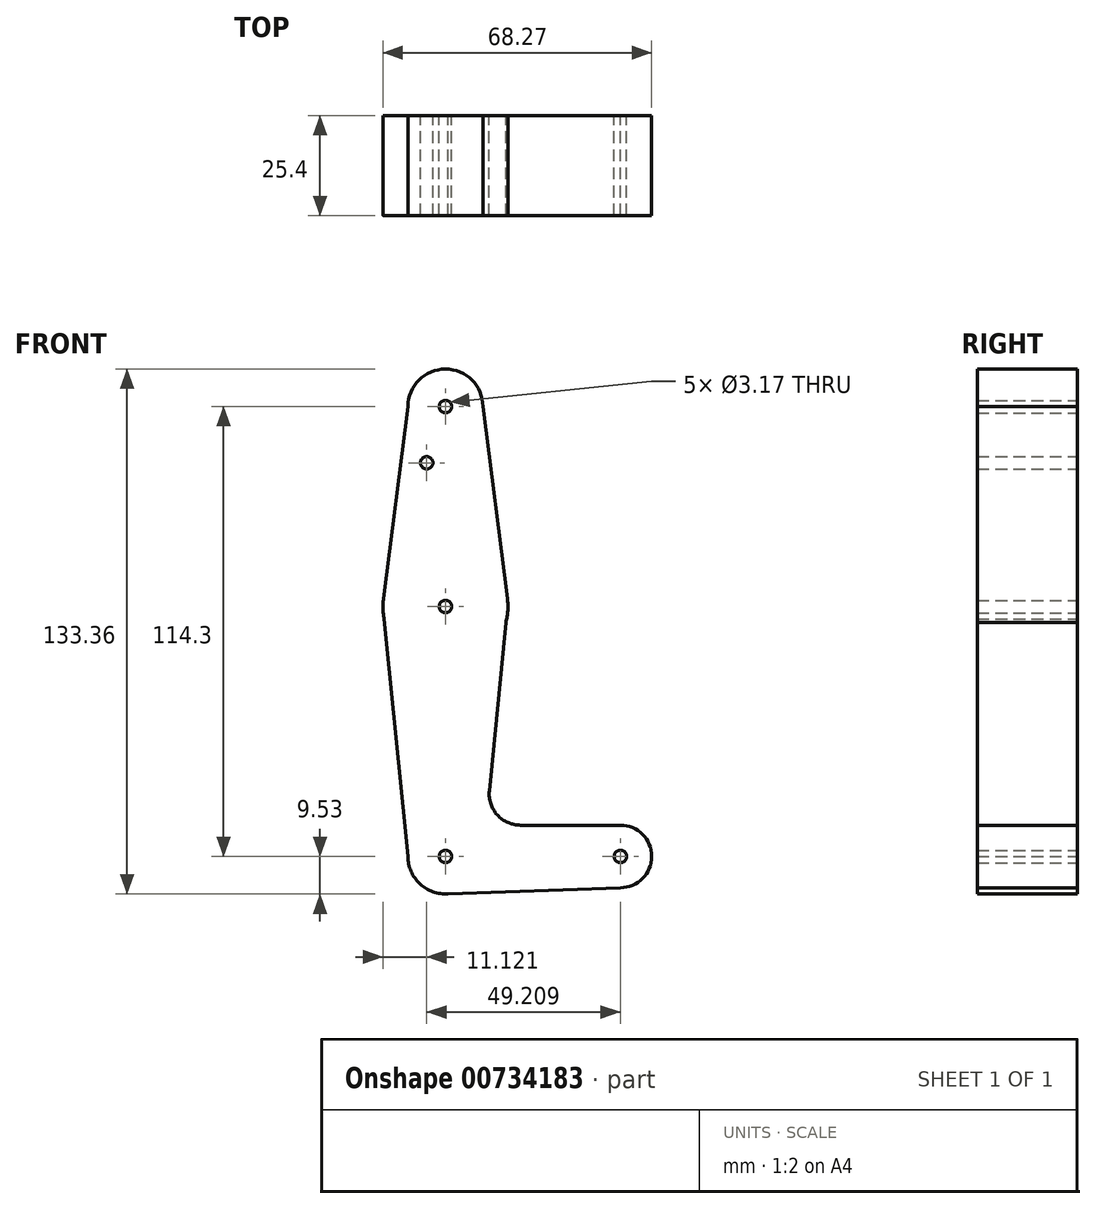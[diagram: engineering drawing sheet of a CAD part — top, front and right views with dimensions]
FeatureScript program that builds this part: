
annotation { "Feature Type Name" : "Feature", "Feature Type Description" : "" }
export const myFeature = defineFeature(function(context is Context, id is Id, definition is map)
    precondition{}
    {
        {
            var Q0;
            Q0=qCreatedBy(makeId("Front.planeOp"),FACE);
            var sketch = newSketch(context, id + "F0", { "sketchPlane" : qUnion([Q0])});
            skPoint(sketch, "E0.start.orphan", {"position": v(0, 0) * mm});
            skLineSegment(sketch, "E1", {"start": v(0, 0) * mm, "end": v(44.45, 0) * mm});
            skCircle(sketch, "E2", {"center": v(0, 114.3) * mm, "radius": 9.53 * mm});
            skCircle(sketch, "E3", {"center": v(0, 0) * mm, "radius": 9.53 * mm});
            skCircle(sketch, "E4", {"center": v(44.45, 0) * mm, "radius": 7.94 * mm});
            skCircle(sketch, "E5", {"center": v(0, 63.5) * mm, "radius": 15.88 * mm});
            skLineSegment(sketch, "E6", {"start": v(0, 0) * mm, "end": v(0, 114.3) * mm});
            skLineSegment(sketch, "E7", {"start": v(-9.52, 114.3) * mm, "end": v(-15.75, 65.5) * mm});
            skLineSegment(sketch, "E8", {"start": v(-15.88, 63.5) * mm, "end": v(-9.52, 0) * mm});
            skPoint(sketch, "E9.start.orphan", {"position": v(0, -9.53) * mm});
            skLineSegment(sketch, "E10", {"start": v(0, -9.53) * mm, "end": v(44.45, -7.94) * mm});
            skLineSegment(sketch, "E11", {"start": v(19.07, 7.94) * mm, "end": v(44.45, 7.94) * mm});
            skLineSegment(sketch, "E12", {"start": v(9.53, 114.3) * mm, "end": v(15.75, 65.5) * mm});
            skLineSegment(sketch, "E13", {"start": v(15.75, 63.5) * mm, "end": v(11.16, 16.66) * mm});
            skArc(sketch, "E14.filletArc", {"start": v(11.16, 16.66) * mm, "mid": v(13.18, 10.55) * mm, "end": v(19.07, 7.94) * mm});
            skCircle(sketch, "E15", {"center": v(-4.76, 100.03) * mm, "radius": 1.59 * mm});
            skCircle(sketch, "E16", {"center": v(0, 114.3) * mm, "radius": 1.59 * mm});
            skCircle(sketch, "E17", {"center": v(0, 63.5) * mm, "radius": 1.59 * mm});
            skCircle(sketch, "E18", {"center": v(0, 0) * mm, "radius": 1.59 * mm});
            skCircle(sketch, "E19", {"center": v(44.45, 0) * mm, "radius": 1.59 * mm});
            skSolve(sketch);
        }
        {
            var Q0;
            Q0 = qSketchRegion(id + "F0", true);
            var Q1;
            {var subQ0=sQuery(id+"F0.wireOp",EDGE,"E18");var subQ1=sQuery(id+"F0.wireOp",EDGE,"E1");var subQ2=makeQuery(id+"F0.imprint","INTERSECT",VERTEX,{"derivedFrom":[subQ1,subQ0]});Q1=makeQuery(id+"F0.imprint","IMPRINT",FACE,{"disambiguationData":[TD([[makeQuery(id+"F0.imprint","IMPRINT",EDGE,{"disambiguationData":[TD([[subQ2,-1.0]])],"derivedFrom":subQ1}),1.0]])]});}
            extrude(context, id + "F1", {"entities" : qUnion([Q0, Q1]), "depth" : 25.4 * mm, "offsetDistance" : 25.4 * mm});
        }
    });
